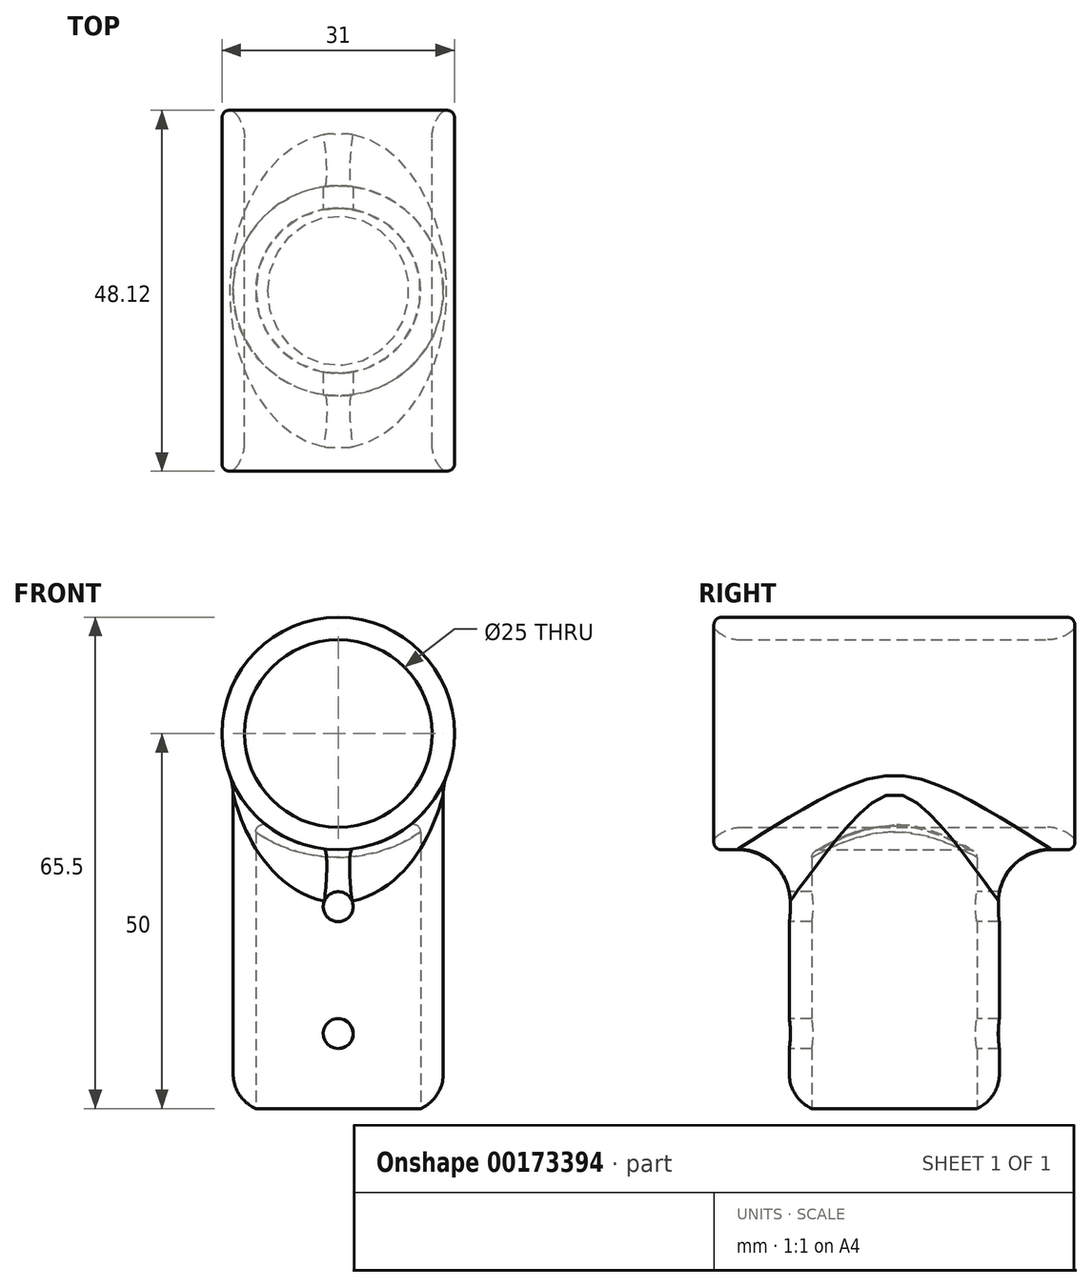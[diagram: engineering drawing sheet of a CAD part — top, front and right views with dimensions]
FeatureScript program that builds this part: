
annotation { "Feature Type Name" : "Feature", "Feature Type Description" : "" }
export const myFeature = defineFeature(function(context is Context, id is Id, definition is map)
    precondition{}
    {
        {
            var Q0;
            Q0=qCreatedBy(makeId("Top.planeOp"),FACE);
            var sketch = newSketch(context, id + "F0", { "sketchPlane" : qUnion([Q0])});
            skCircle(sketch, "E0", {"center": v(0, 0) * mm, "radius": 11 * mm});
            skCircle(sketch, "E1", {"center": v(0, 0) * mm, "radius": 14 * mm});
            skSolve(sketch);
        }
        {
            var Q0;
            Q0 = qSketchRegion(id + "F0", true);
            extrude(context, id + "F1", {"entities" : qUnion([Q0]), "depth" : 40 * mm, "hasSecondDirection" : true, "secondDirectionOppositeDirection" : true, "secondDirectionDepth" : 10 * mm});
        }
        {
            var Q0;
            Q0=qCreatedBy(makeId("Front.planeOp"),FACE);
            var sketch = newSketch(context, id + "F2", { "sketchPlane" : qUnion([Q0])});
            skCircle(sketch, "E2", {"center": v(0, 40) * mm, "radius": 12.5 * mm});
            skCircle(sketch, "E3", {"center": v(0, 40) * mm, "radius": 15.5 * mm});
            skSolve(sketch);
        }
        {
            var Q0;
            Q0=makeQuery(id+"F2.imprint","IMPRINT",FACE,{"disambiguationData":[TD([[makeQuery(id+"F2.imprint","IMPRINT",EDGE,{"derivedFrom":sQuery(id+"F2.wireOp",EDGE,"E2")}),-1.0]])]});
            extrude(context, id + "F3", {"entities" : qUnion([Q0]), "operationType" : NewBodyOperationType.ADD, "depth" : 25 * mm, "hasSecondDirection" : true, "secondDirectionOppositeDirection" : true, "secondDirectionDepth" : 25 * mm});
        }
        {
            var Q0;
            Q0=makeQuery(id+"F2.imprint","IMPRINT",FACE,{"disambiguationData":[TD([[makeQuery(id+"F2.imprint","IMPRINT",EDGE,{"derivedFrom":sQuery(id+"F2.wireOp",EDGE,"E2")}),1.0]])]});
            extrude(context, id + "F4", {"entities" : qUnion([Q0]), "operationType" : NewBodyOperationType.REMOVE, "oppositeDirection" : true, "depth" : 25 * mm, "hasSecondDirection" : true, "secondDirectionOppositeDirection" : false, "secondDirectionDepth" : 25 * mm});
        }
        {
            var Q0;
            Q0=qCreatedBy(makeId("Front.planeOp"),FACE);
            var sketch = newSketch(context, id + "F5", { "sketchPlane" : qUnion([Q0])});
            skCircle(sketch, "E4", {"center": v(0, 16.9) * mm, "radius": 2 * mm});
            skCircle(sketch, "E5", {"center": v(0, 0) * mm, "radius": 2 * mm});
            skSolve(sketch);
        }
        {
            var Q0;
            Q0 = qSketchRegion(id + "F5", true);
            extrude(context, id + "F6", {"entities" : qUnion([Q0]), "operationType" : NewBodyOperationType.REMOVE, "oppositeDirection" : true, "depth" : 25 * mm, "hasSecondDirection" : true, "secondDirectionOppositeDirection" : false, "secondDirectionDepth" : 25 * mm});
        }
        {
            var Q0;
            Q0=makeQuery(id+"F3.opExtrude","CAP_EDGE",EDGE,{"disambiguationData":[OSD([sQuery(id+"F2.wireOp",EDGE,"E2")])],"isStart":true});
            var Q1;
            Q1=makeQuery(id+"F3.opExtrude","CAP_EDGE",EDGE,{"disambiguationData":[OSD([sQuery(id+"F2.wireOp",EDGE,"E2")])],"isStart":false});
            var Q2;
            Q2=makeQuery(id+"F1.opExtrude","CAP_EDGE",EDGE,{"disambiguationData":[OSD([sQuery(id+"F0.wireOp",EDGE,"E1")])],"isStart":true});
            fillet(context, id + "F7", {"entities" : qUnion([Q0, Q1, Q2]), "radius" : 5 * mm, "tangentPropagation" : true, "allowEdgeOverflow" : false});
        }
        {
            var Q0;
            {var subQ0=sQuery(id+"F2.wireOp",EDGE,"E3");var subQ1=sQuery(id+"F2.wireOp",EDGE,"E2");Q0=makeQuery(id+"F7.opFillet","BLEND_EDGE",EDGE,{"blendedFrom":[makeQuery(id+"F3.opExtrude","CAP_EDGE",EDGE,{"disambiguationData":[OSD([subQ1])],"isStart":true}),makeQuery(id+"F3.boolean.opBoolean","SPLIT",FACE,{"disambiguationData":[TD([makeQuery(id+"F1.opExtrude","SWEPT_FACE",FACE,{"disambiguationData":[OSD([sQuery(id+"F0.wireOp",EDGE,"E1")])]})])],"derivedFrom":makeQuery(id+"F3.opExtrude","SWEPT_FACE",FACE,{"disambiguationData":[OSD([subQ0])]})})],"blendedInto":[makeQuery(id+"F3.boolean.opBoolean","SPLIT",FACE,{"disambiguationData":[TD([makeQuery(id+"F1.opExtrude","SWEPT_FACE",FACE,{"disambiguationData":[OSD([sQuery(id+"F0.wireOp",EDGE,"E1")])]})])],"derivedFrom":makeQuery(id+"F3.opExtrude","SWEPT_FACE",FACE,{"disambiguationData":[OSD([subQ0])]})})]});}
            var Q1;
            {var subQ0=sQuery(id+"F2.wireOp",EDGE,"E3");var subQ1=sQuery(id+"F2.wireOp",EDGE,"E2");Q1=makeQuery(id+"F7.opFillet","BLEND_EDGE",EDGE,{"blendedFrom":[makeQuery(id+"F3.opExtrude","CAP_EDGE",EDGE,{"disambiguationData":[OSD([subQ1])],"isStart":false}),makeQuery(id+"F3.boolean.opBoolean","SPLIT",FACE,{"disambiguationData":[TD([makeQuery(id+"F1.opExtrude","SWEPT_FACE",FACE,{"disambiguationData":[OSD([sQuery(id+"F0.wireOp",EDGE,"E1")])]})])],"derivedFrom":makeQuery(id+"F3.opExtrude","SWEPT_FACE",FACE,{"disambiguationData":[OSD([subQ0])]})})],"blendedInto":[makeQuery(id+"F3.boolean.opBoolean","SPLIT",FACE,{"disambiguationData":[TD([makeQuery(id+"F1.opExtrude","SWEPT_FACE",FACE,{"disambiguationData":[OSD([sQuery(id+"F0.wireOp",EDGE,"E1")])]})])],"derivedFrom":makeQuery(id+"F3.opExtrude","SWEPT_FACE",FACE,{"disambiguationData":[OSD([subQ0])]})})]});}
            fillet(context, id + "F8", {"entities" : qUnion([Q0, Q1]), "radius" : 1 * mm, "tangentPropagation" : true, "allowEdgeOverflow" : false});
        }
        {
            var Q0;
            Q0=makeQuery(id+"F3.boolean.opBoolean","INTERSECT",EDGE,{"derivedFrom":[makeQuery(id+"F1.opExtrude","SWEPT_FACE",FACE,{"disambiguationData":[OSD([sQuery(id+"F0.wireOp",EDGE,"E1")])]}),makeQuery(id+"F3.opExtrude","SWEPT_FACE",FACE,{"disambiguationData":[OSD([sQuery(id+"F2.wireOp",EDGE,"E3")])]})]});
            fillet(context, id + "F9", {"entities" : qUnion([Q0]), "radius" : 7 * mm, "tangentPropagation" : true, "allowEdgeOverflow" : false});
        }
        {
            var Q0;
            Q0=makeQuery(id+"F3.boolean.opBoolean","INTERSECT",EDGE,{"derivedFrom":[makeQuery(id+"F1.opExtrude","SWEPT_FACE",FACE,{"disambiguationData":[OSD([sQuery(id+"F0.wireOp",EDGE,"E0")])]}),makeQuery(id+"F3.opExtrude","SWEPT_FACE",FACE,{"disambiguationData":[OSD([sQuery(id+"F2.wireOp",EDGE,"E3")])]})]});
            fillet(context, id + "F10", {"entities" : qUnion([Q0]), "radius" : 1 * mm, "tangentPropagation" : true, "allowEdgeOverflow" : false});
        }
    });
